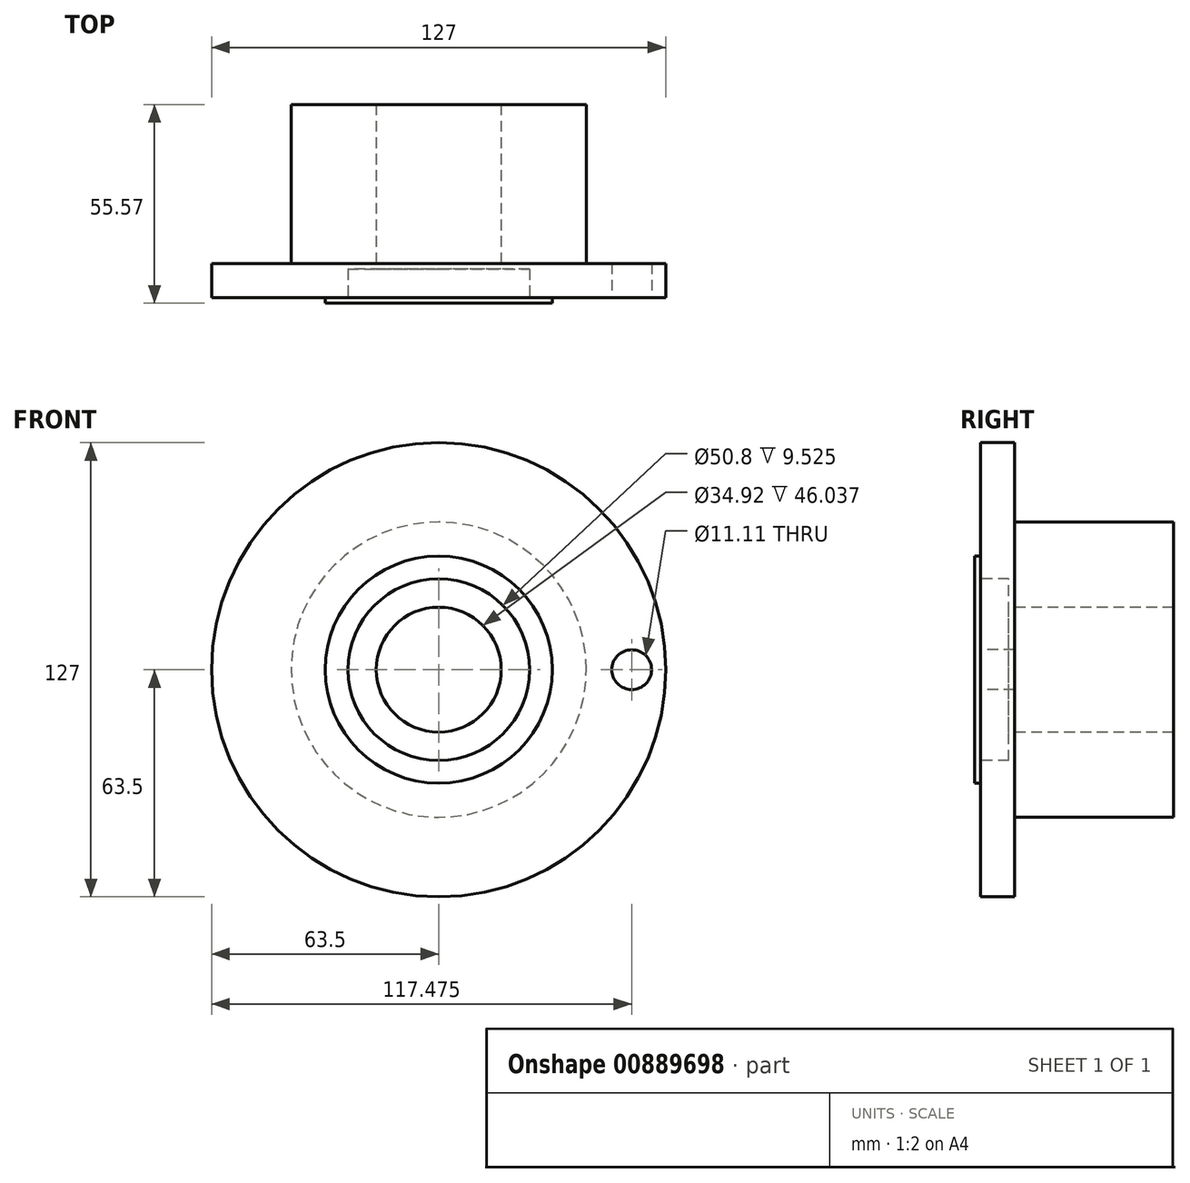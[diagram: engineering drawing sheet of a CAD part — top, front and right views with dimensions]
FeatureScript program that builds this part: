
annotation { "Feature Type Name" : "Feature", "Feature Type Description" : "" }
export const myFeature = defineFeature(function(context is Context, id is Id, definition is map)
    precondition{}
    {
        {
            var Q0;
            Q0=qCreatedBy(makeId("Front.planeOp"),FACE);
            var sketch = newSketch(context, id + "F0", { "sketchPlane" : qUnion([Q0])});
            skCircle(sketch, "E0", {"center": v(0, 0) * mm, "radius": 63.5 * mm});
            skSolve(sketch);
        }
        {
            var Q0;
            Q0 = qSketchRegion(id + "F0", true);
            extrude(context, id + "F1", {"entities" : qUnion([Q0]), "oppositeDirection" : true, "depth" : 9.52 * mm, "offsetDistance" : 25.4 * mm});
        }
        {
            var Q0;
            Q0=makeQuery(id+"F1.opExtrude","CAP_FACE",FACE,{"disambiguationData":[OSD([sQuery(id+"F0.wireOp",EDGE,"E0")])],"isStart":true});
            var sketch = newSketch(context, id + "F2", { "sketchPlane" : qUnion([Q0])});
            skCircle(sketch, "E1", {"center": v(0, 0) * mm, "radius": 31.75 * mm});
            skSolve(sketch);
        }
        {
            var Q0;
            Q0=makeQuery(id+"F2.imprint","IMPRINT",FACE,{"disambiguationData":[TD([[makeQuery(id+"F2.imprint","IMPRINT",EDGE,{"derivedFrom":sQuery(id+"F2.wireOp",EDGE,"E1")}),1.0]])]});
            extrude(context, id + "F3", {"entities" : qUnion([Q0]), "operationType" : NewBodyOperationType.ADD, "depth" : 1.59 * mm, "offsetDistance" : 25.4 * mm});
        }
        {
            var Q0;
            Q0=makeQuery(id+"F3.opExtrude","CAP_FACE",FACE,{"disambiguationData":[OSD([sQuery(id+"F2.wireOp",EDGE,"E1")])],"isStart":false});
            var sketch = newSketch(context, id + "F4", { "sketchPlane" : qUnion([Q0])});
            skCircle(sketch, "E2", {"center": v(0, 0) * mm, "radius": 25.4 * mm});
            skSolve(sketch);
        }
        {
            var Q0;
            Q0=makeQuery(id+"F4.imprint","IMPRINT",FACE,{"disambiguationData":[TD([[makeQuery(id+"F4.imprint","IMPRINT",EDGE,{"derivedFrom":sQuery(id+"F4.wireOp",EDGE,"E2")}),1.0]])]});
            extrude(context, id + "F5", {"entities" : qUnion([Q0]), "operationType" : NewBodyOperationType.REMOVE, "oppositeDirection" : true, "depth" : 9.52 * mm, "offsetDistance" : 25.4 * mm});
        }
        {
            var Q0;
            Q0=makeQuery(id+"F1.opExtrude","CAP_FACE",FACE,{"disambiguationData":[OSD([sQuery(id+"F0.wireOp",EDGE,"E0")])],"isStart":false});
            var sketch = newSketch(context, id + "F6", { "sketchPlane" : qUnion([Q0])});
            skCircle(sketch, "E3", {"center": v(0, 0) * mm, "radius": 41.28 * mm});
            skSolve(sketch);
        }
        {
            var Q0;
            Q0 = qSketchRegion(id + "F6", true);
            extrude(context, id + "F7", {"entities" : qUnion([Q0]), "operationType" : NewBodyOperationType.ADD, "depth" : 44.45 * mm, "offsetDistance" : 25.4 * mm});
        }
        {
            var Q0;
            Q0=makeQuery(id+"F3.opExtrude","CAP_FACE",FACE,{"disambiguationData":[OSD([sQuery(id+"F2.wireOp",EDGE,"E1")])],"isStart":false});
            var sketch = newSketch(context, id + "F8", { "sketchPlane" : qUnion([Q0])});
            skCircle(sketch, "E4", {"center": v(0, 0) * mm, "radius": 17.46 * mm});
            skSolve(sketch);
        }
        {
            var Q0;
            Q0 = qSketchRegion(id + "F8", true);
            extrude(context, id + "F9", {"entities" : qUnion([Q0]), "operationType" : NewBodyOperationType.REMOVE, "endBound" : BoundingType.THROUGH_ALL, "oppositeDirection" : true, "depth" : 25.4 * mm, "offsetDistance" : 25.4 * mm});
        }
        {
            var Q0;
            Q0=makeQuery(id+"F1.opExtrude","CAP_FACE",FACE,{"disambiguationData":[OSD([sQuery(id+"F0.wireOp",EDGE,"E0")])],"isStart":true});
            var sketch = newSketch(context, id + "F10", { "sketchPlane" : qUnion([Q0])});
            skCircle(sketch, "E5", {"center": v(0, 0) * mm, "radius": 53.98 * mm, "construction": true});
            skCircle(sketch, "E6", {"center": v(53.98, 0) * mm, "radius": 5.56 * mm});
            skSolve(sketch);
        }
        {
            var Q0;
            Q0=makeQuery(id+"F10.imprint","IMPRINT",FACE,{"disambiguationData":[TD([[makeQuery(id+"F10.imprint","IMPRINT",EDGE,{"derivedFrom":sQuery(id+"F10.wireOp",EDGE,"E6")}),1.0]])]});
            extrude(context, id + "F11", {"entities" : qUnion([Q0]), "operationType" : NewBodyOperationType.REMOVE, "endBound" : BoundingType.THROUGH_ALL, "oppositeDirection" : true, "depth" : 25.4 * mm, "offsetDistance" : 25.4 * mm});
        }
    });
